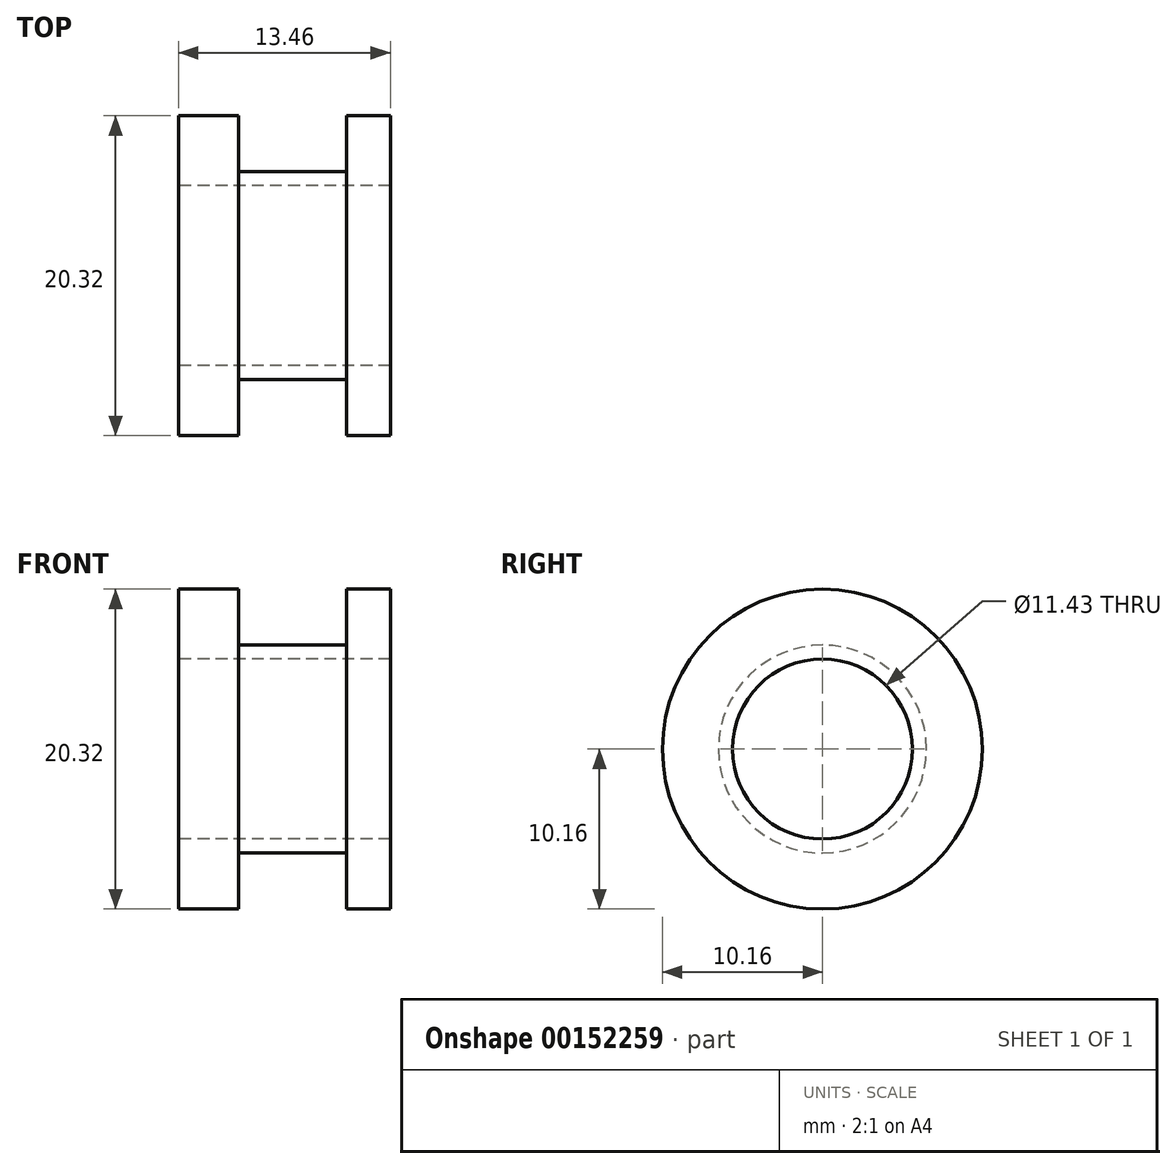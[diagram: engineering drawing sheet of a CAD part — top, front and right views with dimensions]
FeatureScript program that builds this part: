
annotation { "Feature Type Name" : "Feature", "Feature Type Description" : "" }
export const myFeature = defineFeature(function(context is Context, id is Id, definition is map)
    precondition{}
    {
        {
            var Q0;
            Q0=qCreatedBy(makeId("Front.planeOp"),FACE);
            var sketch = newSketch(context, id + "F0", { "sketchPlane" : qUnion([Q0])});
            skLineSegment(sketch, "E0", {"start": v(0, 0) * mm, "end": v(0, 10.16) * mm});
            skLineSegment(sketch, "E1", {"start": v(0, 10.16) * mm, "end": v(3.8, 10.16) * mm});
            skLineSegment(sketch, "E2", {"start": v(3.8, 10.16) * mm, "end": v(3.8, 6.6) * mm});
            skLineSegment(sketch, "E3", {"start": v(3.81, 6.6) * mm, "end": v(10.67, 6.6) * mm});
            skLineSegment(sketch, "E4", {"start": v(10.67, 6.6) * mm, "end": v(10.67, 10.16) * mm});
            skLineSegment(sketch, "E5", {"start": v(10.67, 10.16) * mm, "end": v(13.46, 10.16) * mm});
            skLineSegment(sketch, "E6", {"start": v(13.46, 10.16) * mm, "end": v(13.46, 0) * mm});
            skLineSegment(sketch, "E7", {"start": v(13.46, 0) * mm, "end": v(0, 0) * mm});
            skSolve(sketch);
        }
        {
            var Q0;
            Q0 = qSketchRegion(id + "F0", true);
            var Q1;
            Q1=sQuery(id+"F0.wireOp",EDGE,"E7");
            revolve(context, id + "F1", {"entities" : qUnion([Q0]), "axis" : qUnion([Q1]), "revolveType" : RevolveType.FULL});
        }
        {
            var Q0;
            Q0=qCreatedBy(makeId("Right.planeOp"),FACE);
            var sketch = newSketch(context, id + "F2", { "sketchPlane" : qUnion([Q0])});
            skCircle(sketch, "E8", {"center": v(0, 0) * mm, "radius": 5.72 * mm});
            skSolve(sketch);
        }
        {
            var Q0;
            Q0 = qSketchRegion(id + "F2", true);
            extrude(context, id + "F3", {"entities" : qUnion([Q0]), "operationType" : NewBodyOperationType.REMOVE, "endBound" : BoundingType.THROUGH_ALL, "depth" : 25.4 * mm});
        }
    });
